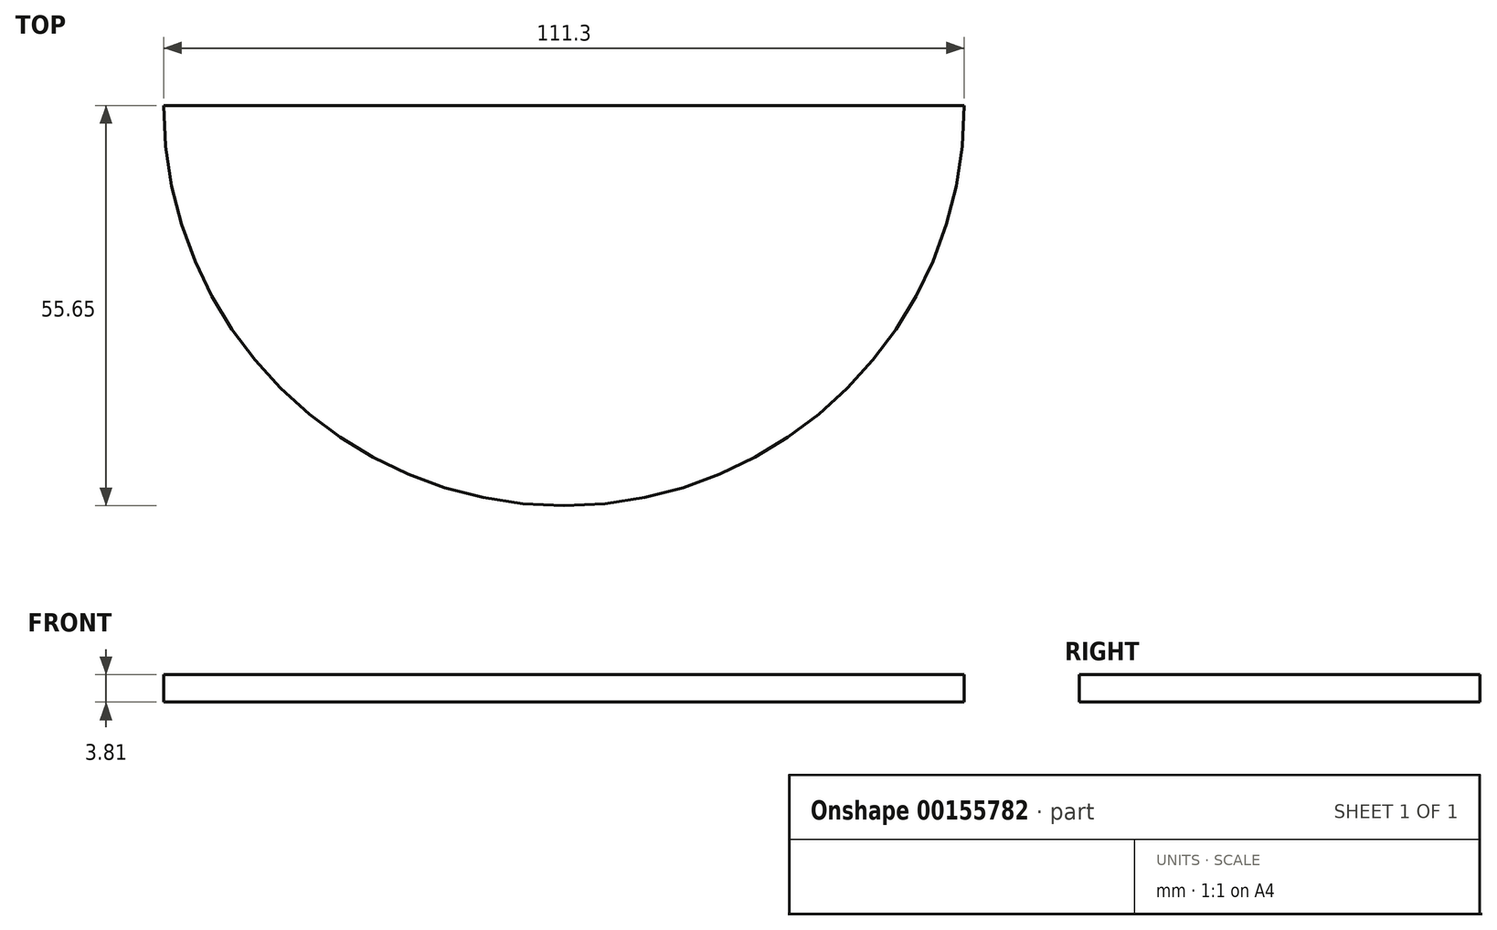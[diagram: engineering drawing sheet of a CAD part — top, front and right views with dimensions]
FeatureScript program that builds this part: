
annotation { "Feature Type Name" : "Feature", "Feature Type Description" : "" }
export const myFeature = defineFeature(function(context is Context, id is Id, definition is map)
    precondition{}
    {
        {
            var Q0;
            Q0=qCreatedBy(makeId("Top.planeOp"),FACE);
            var sketch = newSketch(context, id + "F0", { "sketchPlane" : qUnion([Q0])});
            skArc(sketch, "E0", {"start": v(-55.65, 0) * mm, "mid": v(0, -55.65) * mm, "end": v(55.65, 0) * mm});
            skLineSegment(sketch, "E1", {"start": v(-55.65, 0) * mm, "end": v(55.65, 0) * mm});
            skSolve(sketch);
        }
        {
            var Q0;
            Q0=makeQuery(id+"F0.imprint","IMPRINT",FACE,{"disambiguationData":[TD([[makeQuery(id+"F0.imprint","IMPRINT",EDGE,{"derivedFrom":sQuery(id+"F0.wireOp",EDGE,"E0")}),1.0]])]});
            extrude(context, id + "F1", {"entities" : qUnion([Q0]), "depth" : 3.8 * mm});
        }
    });
